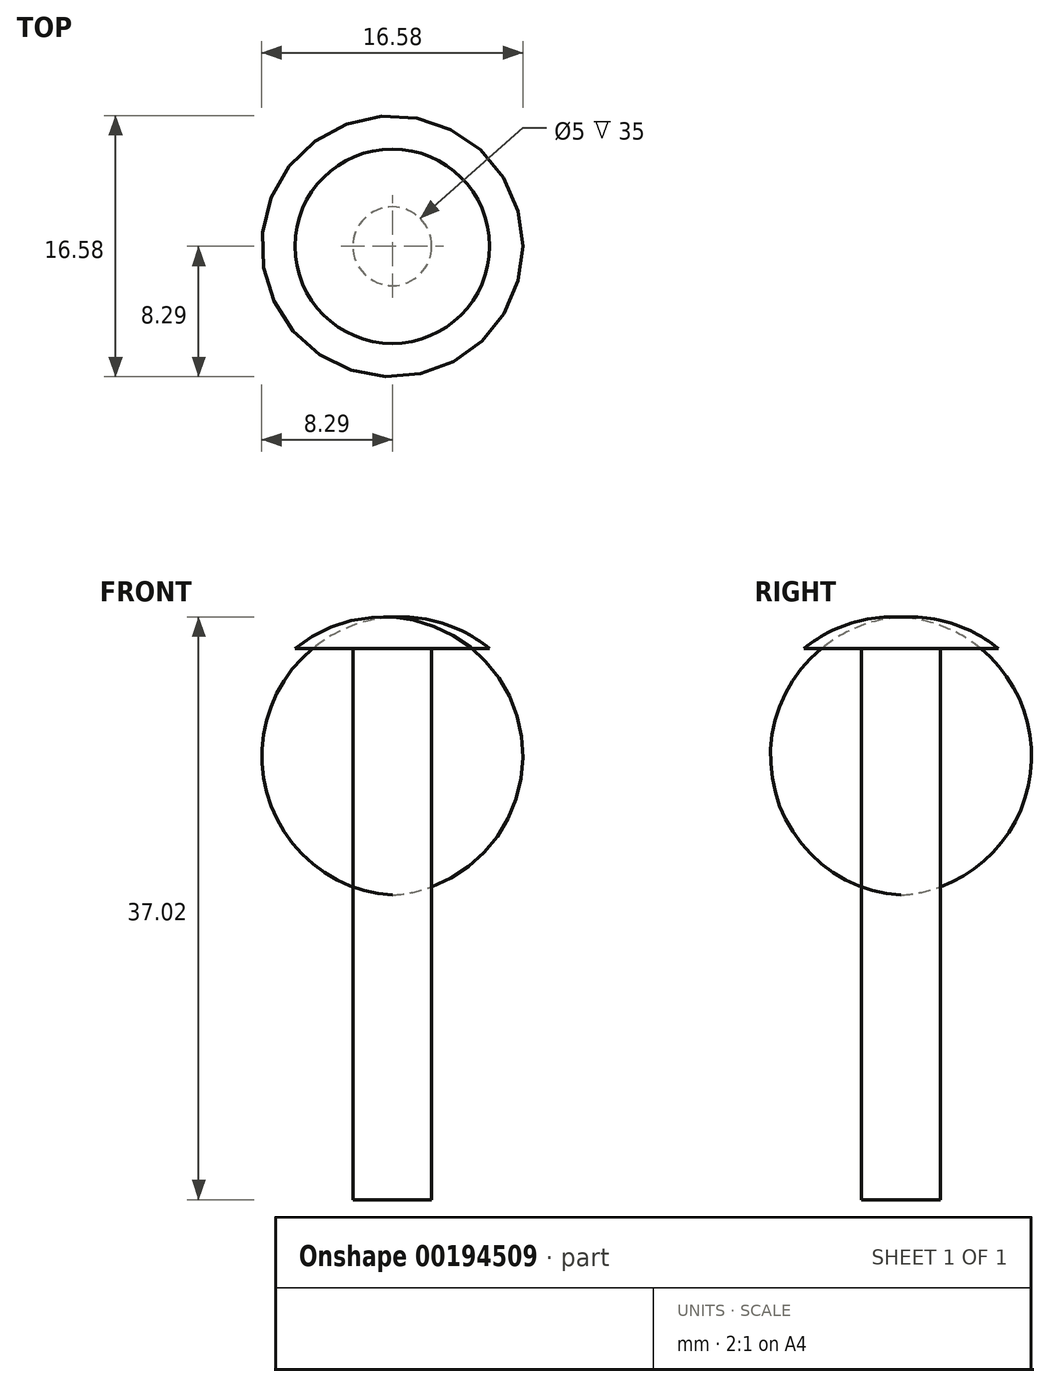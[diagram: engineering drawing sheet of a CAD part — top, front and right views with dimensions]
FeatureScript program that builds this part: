
annotation { "Feature Type Name" : "Feature", "Feature Type Description" : "" }
export const myFeature = defineFeature(function(context is Context, id is Id, definition is map)
    precondition{}
    {
        {
            var Q0;
            Q0=qCreatedBy(makeId("Front.planeOp"),FACE);
            var sketch = newSketch(context, id + "F0", { "sketchPlane" : qUnion([Q0])});
            skLineSegment(sketch, "E0", {"start": v(0, 0) * mm, "end": v(6.18, 0) * mm});
            skLineSegment(sketch, "E1", {"start": v(0, 0) * mm, "end": v(0, 2) * mm});
            skArc(sketch, "E2", {"start": v(6.18, 0) * mm, "mid": v(3.28, 1.59) * mm, "end": v(0, 2) * mm});
            skSolve(sketch);
        }
        {
            var Q0;
            Q0=makeQuery(id+"F0.imprint","IMPRINT",FACE,{"disambiguationData":[TD([[makeQuery(id+"F0.imprint","IMPRINT",EDGE,{"derivedFrom":sQuery(id+"F0.wireOp",EDGE,"E0")}),1.0]])]});
            var Q1;
            Q1=sQuery(id+"F0.wireOp",EDGE,"E1");
            revolve(context, id + "F1", {"entities" : qUnion([Q0]), "axis" : qUnion([Q1]), "revolveType" : RevolveType.FULL});
        }
        {
            var Q0;
            Q0=makeQuery(id+"F1.opRevolve","SWEPT_FACE",FACE,{"disambiguationData":[OSD([sQuery(id+"F0.wireOp",EDGE,"E0")])]});
            var sketch = newSketch(context, id + "F2", { "sketchPlane" : qUnion([Q0])});
            skCircle(sketch, "E3", {"center": v(0, 0) * mm, "radius": 2.5 * mm});
            skSolve(sketch);
        }
        {
            var Q0;
            Q0 = qSketchRegion(id + "F2", true);
            var Q1;
            Q1=makeQuery(id+"F2.imprint","IMPRINT",FACE,{"disambiguationData":[TD([[makeQuery(id+"F2.imprint","IMPRINT",EDGE,{"derivedFrom":sQuery(id+"F2.wireOp",EDGE,"E3")}),1.0]])]});
            extrude(context, id + "F3", {"entities" : qUnion([Q0, Q1]), "operationType" : NewBodyOperationType.ADD, "depth" : 35 * mm});
        }
    });
